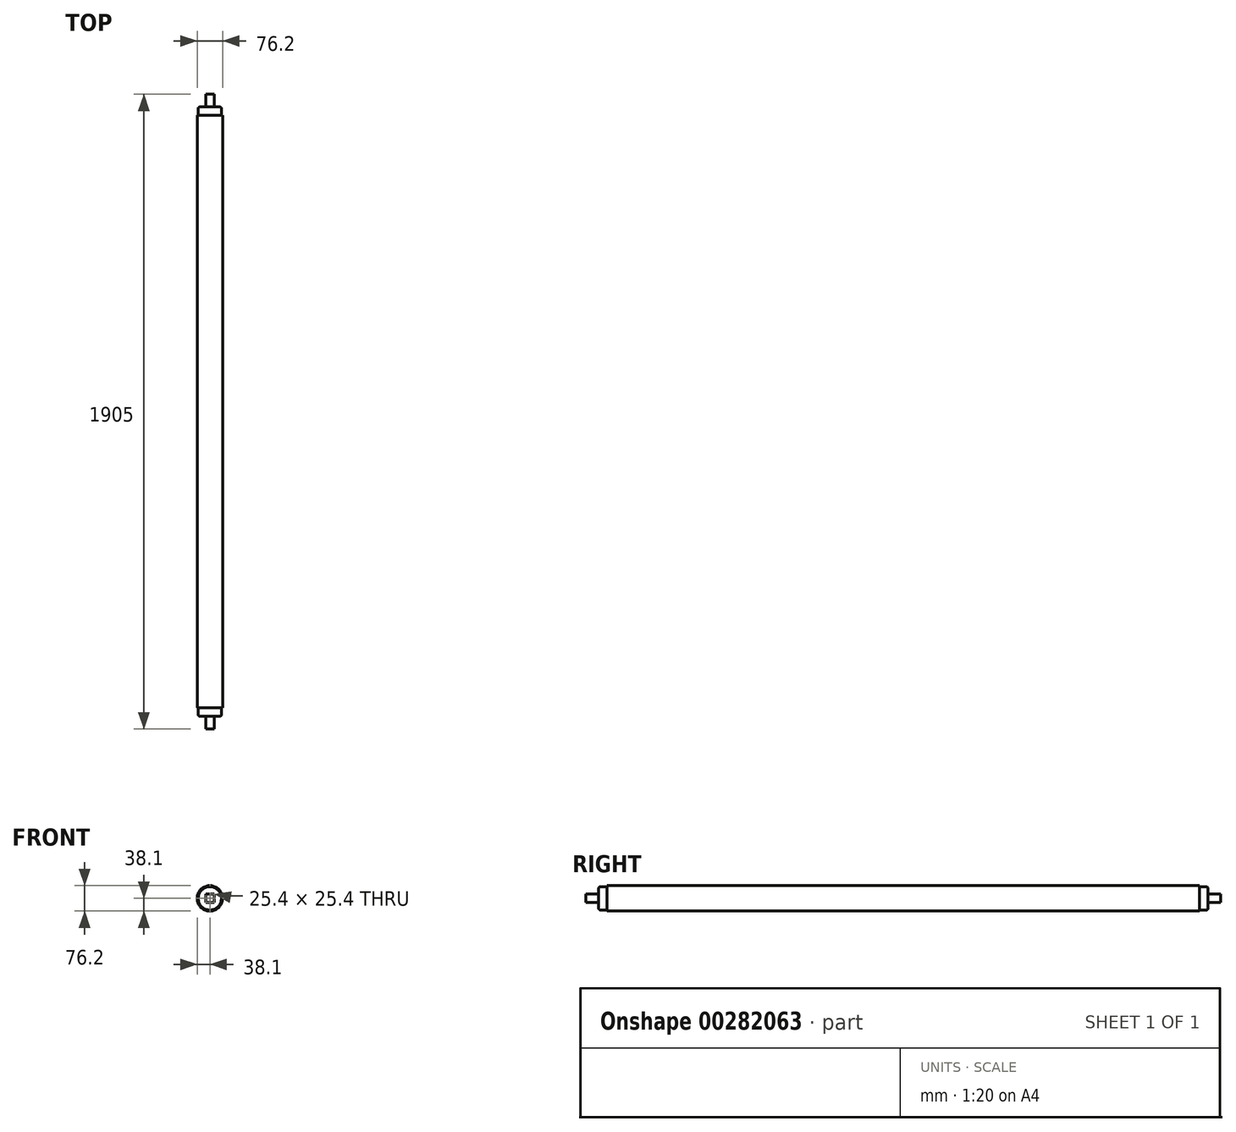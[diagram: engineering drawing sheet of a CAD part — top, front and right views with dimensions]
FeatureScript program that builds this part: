
annotation { "Feature Type Name" : "Feature", "Feature Type Description" : "" }
export const myFeature = defineFeature(function(context is Context, id is Id, definition is map)
    precondition{}
    {
        {
            var Q0;
            Q0=qCreatedBy(makeId("Front.planeOp"),FACE);
            var sketch = newSketch(context, id + "F0", { "sketchPlane" : qUnion([Q0])});
            skCircle(sketch, "E0", {"center": v(0, 0) * mm, "radius": 38.1 * mm});
            skSolve(sketch);
        }
        {
            var Q0;
            Q0 = qSketchRegion(id + "F0", true);
            extrude(context, id + "F1", {"entities" : qUnion([Q0]), "depth" : 1778 * mm});
        }
        {
            var Q0;
            Q0=makeQuery(id+"F1.opExtrude","CAP_FACE",FACE,{"disambiguationData":[OSD([sQuery(id+"F0.wireOp",EDGE,"E0")])],"isStart":false});
            var sketch = newSketch(context, id + "F2", { "sketchPlane" : qUnion([Q0])});
            skCircle(sketch, "E1", {"center": v(0, 0) * mm, "radius": 34.93 * mm});
            skSolve(sketch);
        }
        {
            var Q0;
            Q0 = qSketchRegion(id + "F2", true);
            extrude(context, id + "F3", {"entities" : qUnion([Q0]), "operationType" : NewBodyOperationType.ADD, "depth" : 25.4 * mm});
        }
        {
            var Q0;
            Q0=makeQuery(id+"F1.opExtrude","CAP_FACE",FACE,{"disambiguationData":[OSD([sQuery(id+"F0.wireOp",EDGE,"E0")])],"isStart":true});
            var sketch = newSketch(context, id + "F4", { "sketchPlane" : qUnion([Q0])});
            skCircle(sketch, "E2", {"center": v(0, 0) * mm, "radius": 34.93 * mm});
            skSolve(sketch);
        }
        {
            var Q0;
            Q0 = qSketchRegion(id + "F4", true);
            extrude(context, id + "F5", {"entities" : qUnion([Q0]), "operationType" : NewBodyOperationType.ADD, "depth" : 25.4 * mm});
        }
        {
            var Q0;
            Q0=makeQuery(id+"F3.opExtrude","CAP_FACE",FACE,{"disambiguationData":[OSD([sQuery(id+"F2.wireOp",EDGE,"E1")])],"isStart":false});
            var sketch = newSketch(context, id + "F6", { "sketchPlane" : qUnion([Q0])});
            skLineSegment(sketch, "E3.bottom", {"start": v(12.7, 12.7) * mm, "end": v(-12.7, 12.7) * mm});
            skLineSegment(sketch, "E3.top", {"start": v(12.7, -12.7) * mm, "end": v(-12.7, -12.7) * mm});
            skLineSegment(sketch, "E3.left", {"start": v(12.7, 12.7) * mm, "end": v(12.7, -12.7) * mm});
            skLineSegment(sketch, "E3.right", {"start": v(-12.7, 12.7) * mm, "end": v(-12.7, -12.7) * mm});
            skPoint(sketch, "E3.middle", {"position": v(0, 0) * mm});
            skSolve(sketch);
        }
        {
            var Q0;
            Q0 = qSketchRegion(id + "F6", true);
            extrude(context, id + "F7", {"entities" : qUnion([Q0]), "operationType" : NewBodyOperationType.ADD, "depth" : 38.1 * mm});
        }
        {
            var Q0;
            Q0=makeQuery(id+"F5.opExtrude","CAP_FACE",FACE,{"disambiguationData":[OSD([sQuery(id+"F4.wireOp",EDGE,"E2")])],"isStart":false});
            var sketch = newSketch(context, id + "F8", { "sketchPlane" : qUnion([Q0])});
            skLineSegment(sketch, "E4.bottom", {"start": v(12.7, 12.7) * mm, "end": v(-12.7, 12.7) * mm});
            skLineSegment(sketch, "E4.top", {"start": v(12.7, -12.7) * mm, "end": v(-12.7, -12.7) * mm});
            skLineSegment(sketch, "E4.left", {"start": v(12.7, 12.7) * mm, "end": v(12.7, -12.7) * mm});
            skLineSegment(sketch, "E4.right", {"start": v(-12.7, 12.7) * mm, "end": v(-12.7, -12.7) * mm});
            skPoint(sketch, "E4.middle", {"position": v(0, 0) * mm});
            skSolve(sketch);
        }
        {
            var Q0;
            Q0=makeQuery(id+"F8.imprint","IMPRINT",FACE,{"disambiguationData":[TD([[makeQuery(id+"F8.imprint","IMPRINT",EDGE,{"derivedFrom":sQuery(id+"F8.wireOp",EDGE,"E4.bottom")}),1.0]])]});
            extrude(context, id + "F9", {"entities" : qUnion([Q0]), "operationType" : NewBodyOperationType.ADD, "flatOperationType" : FlatOperationType.REMOVE, "offsetDistance" : 25.4 * mm, "depth" : 38.1 * mm, "domain" : OperationDomain.MODEL});
        }
        {
            var Q0;
            Q0=makeQuery(id+"F5.opExtrude","CAP_EDGE",EDGE,{"disambiguationData":[OSD([sQuery(id+"F4.wireOp",EDGE,"E2")])],"isStart":false});
            fillet(context, id + "F10", {"entities" : qUnion([Q0]), "radius" : 5.08 * mm, "tangentPropagation" : true, "allowEdgeOverflow" : false});
        }
        {
            var Q0;
            Q0=makeQuery(id+"F3.opExtrude","CAP_EDGE",EDGE,{"disambiguationData":[OSD([sQuery(id+"F2.wireOp",EDGE,"E1")])],"isStart":false});
            fillet(context, id + "F11", {"entities" : qUnion([Q0]), "radius" : 5.08 * mm, "tangentPropagation" : true, "allowEdgeOverflow" : false});
        }
    });
